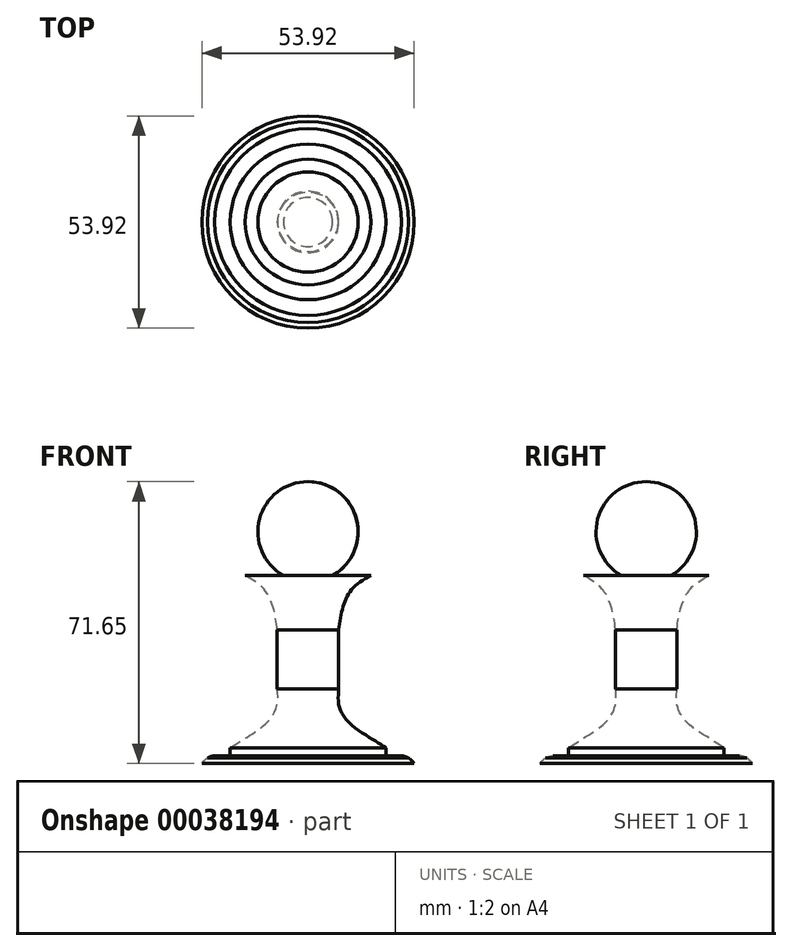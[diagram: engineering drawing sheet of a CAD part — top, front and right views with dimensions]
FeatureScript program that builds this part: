
annotation { "Feature Type Name" : "Feature", "Feature Type Description" : "" }
export const myFeature = defineFeature(function(context is Context, id is Id, definition is map)
    precondition{}
    {
        {
            var Q0;
            Q0=qCreatedBy(makeId("Front.planeOp"),FACE);
            var sketch = newSketch(context, id + "F0", { "sketchPlane" : qUnion([Q0])});
            skLineSegment(sketch, "E0", {"start": v(0, 24.96) * mm, "end": v(0, 0) * mm});
            skLineSegment(sketch, "E1", {"start": v(6.24, 13.85) * mm, "end": v(15.97, 13.85) * mm});
            skLineSegment(sketch, "E2", {"start": v(7.81, 0) * mm, "end": v(7.81, -15) * mm});
            skLineSegment(sketch, "E3", {"start": v(0, -15) * mm, "end": v(0, -33.95) * mm});
            skLineSegment(sketch, "E4", {"start": v(0, -33.95) * mm, "end": v(26.96, -33.95) * mm});
            skLineSegment(sketch, "E5", {"start": v(19.75, -31.95) * mm, "end": v(23.7, -31.95) * mm});
            skArc(sketch, "E6", {"start": v(6.24, 13.85) * mm, "mid": v(12.33, 28.19) * mm, "end": v(0, 37.7) * mm});
            skFitSpline(sketch, "E7", {"points": [v(15.97, 13.85) * mm, v(12.03, 11.25) * mm, v(9.82, 8.28) * mm, v(8.55, 4.56) * mm, v(7.81, 0) * mm], "startDerivative": vector(-16.23, -9.22) * mm, "endDerivative": vector(-1.53, -17.9) * mm});
            skLineSegment(sketch, "E8", {"start": v(19.75, -29.97) * mm, "end": v(19.75, -31.95) * mm});
            skLineSegment(sketch, "E9", {"start": v(0, 24.96) * mm, "end": v(0, 37.7) * mm});
            skFitSpline(sketch, "E10", {"points": [v(23.7, -31.95) * mm, v(24.75, -32.2) * mm, v(25.55, -32.54) * mm], "startDerivative": vector(1.62, -0.21) * mm, "endDerivative": vector(1.57, -0.79) * mm});
            skFitSpline(sketch, "E11", {"points": [v(25.55, -32.54) * mm, v(26.28, -33.07) * mm, v(26.96, -33.95) * mm], "startDerivative": vector(1.59, -0.97) * mm, "endDerivative": vector(1.23, -1.82) * mm});
            skFitSpline(sketch, "E12", {"points": [v(7.81, -15) * mm, v(7.81, -18.86) * mm, v(10.24, -23.37) * mm, v(16.07, -27.57) * mm, v(19.75, -29.97) * mm], "startDerivative": vector(-1.73, -17.48) * mm, "endDerivative": vector(14.3, -10.12) * mm});
            skPoint(sketch, "E13.orphan", {"position": v(0, 13.85) * mm});
            skLineSegment(sketch, "E14", {"start": v(0, 0) * mm, "end": v(0, -15) * mm});
            skSolve(sketch);
        }
        {
            var Q0;
            Q0=makeQuery(id+"F0.imprint","IMPRINT",FACE,{"disambiguationData":[TD([[makeQuery(id+"F0.imprint","IMPRINT",EDGE,{"derivedFrom":sQuery(id+"F0.wireOp",EDGE,"E0")}),1.0]])]});
            var Q1;
            Q1=sQuery(id+"F0.wireOp",EDGE,"E3");
            revolve(context, id + "F1", {"entities" : qUnion([Q0]), "axis" : qUnion([Q1]), "revolveType" : RevolveType.FULL});
        }
    });
